# Revit family: Haworth_XSeries_ComboUnit_5High
name_source: partatom
category: Furniture Systems
revit_build: Autodesk Revit 2018 (Build: 20170223_1515(x64)
units: mm (PartAtom-declared; Revit-internal decimal feet)

## family parameters
Always vertical = Yes
Cut with Voids When Loaded = No
OmniClass Number = 23.40.70.14.64.21
OmniClass Title = Systems Furniture
Part Type = Normal
Room Calculation Point = No
Round Connector Dimension = Use Diameter
Shared = No
Work Plane-Based = No

## types (6) — shared parameters
Actual Depth = 18 3/4"
Actual Height = 63 1/2"
Assembly Code = E2020200
Base Height = 2"
Classic Pull = No
Crescent Pull = No
Custom Size = No
Description = Haworth XSeries Combo Unit
Drawer 1 Height = 12"
Drawer 2 Height = 12"
Ellipse Pull = No
J Pull = No
Linear Pull = Yes
Manufacturer = Haworth
Max. Height = 63 1/2"
Max. Width = 42"
Min. Height = 27 1/2"
Min. Width = 30"
Model = JCPX
Pull Finish = Haworth _ Metal _ Brushed Aluminum
Radius Pull = No
Revision Number = 2
Shelf Depth = 17 1/4"
Standard Widths = 30, 36, 42 in.
Sustainability Info = https://www.haworth.com
Taper Pull = No
Top Thickness = 1 1/4"
URL = http://www.haworth.com
URL - Product = https://www.haworth.com
Verify Final Dim. w/ Haworth = Verify Final Dim. w/ Haworth
Warranty = http://www.haworth.com

## per-type parameters (varying)
| type | Actual Top Cabinet Height | Actual Width | Bottom Cabinet Height | Door Height | Door Width | Double Drawer | Double Shelf | Drawer Width | Pull Height Centerline | Shelf 1 Height | Shelf 2 Height | Shelf Width | Triple Drawer | Width |
| 18d 30w 63h - Triple Drawers | 23 3/4" | 29 7/8" | 38 1/2" | 23 5/8" | 14 7/8" | No | No | 29 7/8" | 11 13/16" | 11 7/8" | 15 213/256" | 28 3/8" | Yes | 30" |
| 18d 30w 63h - Double Drawers | 35 7/8" | 29 7/8" | 26 3/8" | 35 3/4" | 14 7/8" | Yes | Yes | 29 7/8" | 17 7/8" | 11 245/256" | 23 235/256" | 28 3/8" | No | 30" |
| 18d 36w 63h - Triple Drawers | 23 3/4" | 35 7/8" | 38 1/2" | 23 5/8" | 17 7/8" | No | No | 35 7/8" | 11 13/16" | 11 7/8" | 15 213/256" | 34 3/8" | Yes | 36" |
| 18d 36w 63h - Double Drawers | 35 7/8" | 35 7/8" | 26 3/8" | 35 3/4" | 17 7/8" | Yes | Yes | 35 7/8" | 17 7/8" | 11 245/256" | 23 235/256" | 34 3/8" | No | 36" |
| 18d 42w 63h - Triple Drawers | 23 3/4" | 41 7/8" | 38 1/2" | 23 5/8" | 20 7/8" | No | No | 41 7/8" | 11 13/16" | 11 7/8" | 15 213/256" | 40 3/8" | Yes | 42" |
| 18d 42w 63h - Double Drawers | 35 7/8" | 41 7/8" | 26 3/8" | 35 3/4" | 20 7/8" | Yes | Yes | 41 7/8" | 17 7/8" | 11 245/256" | 23 235/256" | 40 3/8" | No | 42" |

## geometry (parser evidence)
native form markers: Sweep x15
no freeform markers — native parametric forms only
